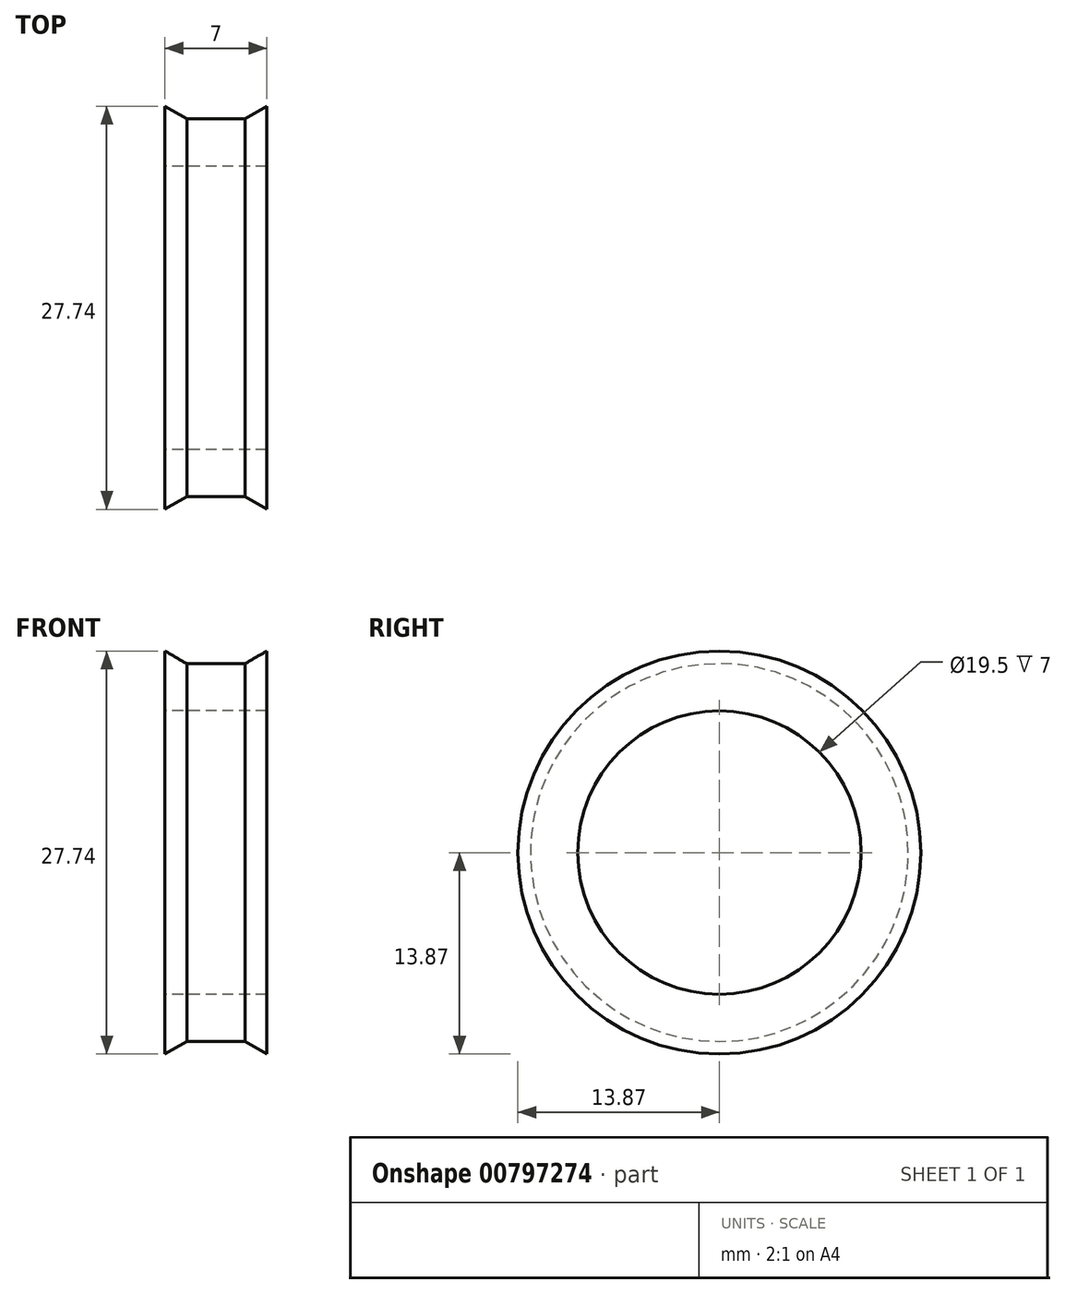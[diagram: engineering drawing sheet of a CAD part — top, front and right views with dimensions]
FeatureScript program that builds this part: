
annotation { "Feature Type Name" : "Feature", "Feature Type Description" : "" }
export const myFeature = defineFeature(function(context is Context, id is Id, definition is map)
    precondition{}
    {
        {
            var Q0;
            Q0=qCreatedBy(makeId("Top.planeOp"),FACE);
            var sketch = newSketch(context, id + "F0", { "sketchPlane" : qUnion([Q0])});
            skLineSegment(sketch, "E0.bottom", {"start": v(0, 0) * mm, "end": v(7, 0) * mm});
            skLineSegment(sketch, "E0.top", {"start": v(0, 14) * mm, "end": v(7, 14) * mm});
            skLineSegment(sketch, "E0.left", {"start": v(0, 0) * mm, "end": v(0, 14) * mm});
            skLineSegment(sketch, "E0.right", {"start": v(7, 0) * mm, "end": v(7, 14) * mm});
            skLineSegment(sketch, "E1.bottom", {"start": v(1.22, 13) * mm, "end": v(5.78, 13) * mm, "construction": true});
            skLineSegment(sketch, "E1.top", {"start": v(1.22, 0) * mm, "end": v(5.78, 0) * mm, "construction": true});
            skLineSegment(sketch, "E1.left", {"start": v(1.22, 13) * mm, "end": v(1.22, 0) * mm, "construction": true});
            skLineSegment(sketch, "E1.right", {"start": v(5.78, 13) * mm, "end": v(5.78, 0) * mm, "construction": true});
            skLineSegment(sketch, "E2", {"start": v(3.5, 13) * mm, "end": v(3.5, 6.3) * mm, "construction": true});
            skLineSegment(sketch, "E3", {"start": v(3.5, 13.45) * mm, "end": v(3.5, 14) * mm, "construction": true});
            skLineSegment(sketch, "E4", {"start": v(1.5, 13) * mm, "end": v(-0.23, 14) * mm});
            skLineSegment(sketch, "E5", {"start": v(5.5, 13) * mm, "end": v(7.23, 14) * mm});
            skLineSegment(sketch, "E6", {"start": v(1.5, 13) * mm, "end": v(5.5, 13) * mm});
            skLineSegment(sketch, "E7", {"start": v(0, 9.75) * mm, "end": v(7, 9.75) * mm});
            skSolve(sketch);
        }
        {
            var Q0;
            {var subQ0=sQuery(id+"F0.wireOp",EDGE,"E6");Q0=makeQuery(id+"F0.imprint","IMPRINT",FACE,{"disambiguationData":[TD([[makeQuery(id+"F0.imprint","IMPRINT",EDGE,{"derivedFrom":subQ0}),-1.0]])]});}
            var Q1;
            Q1=sQuery(id+"F0.wireOp",EDGE,"E0.bottom");
            revolve(context, id + "F1", {"surfaceOperationType" : NewSurfaceOperationType.NEW, "entities" : qUnion([Q0]), "axis" : qUnion([Q1]), "revolveType" : RevolveType.FULL});
        }
    });
